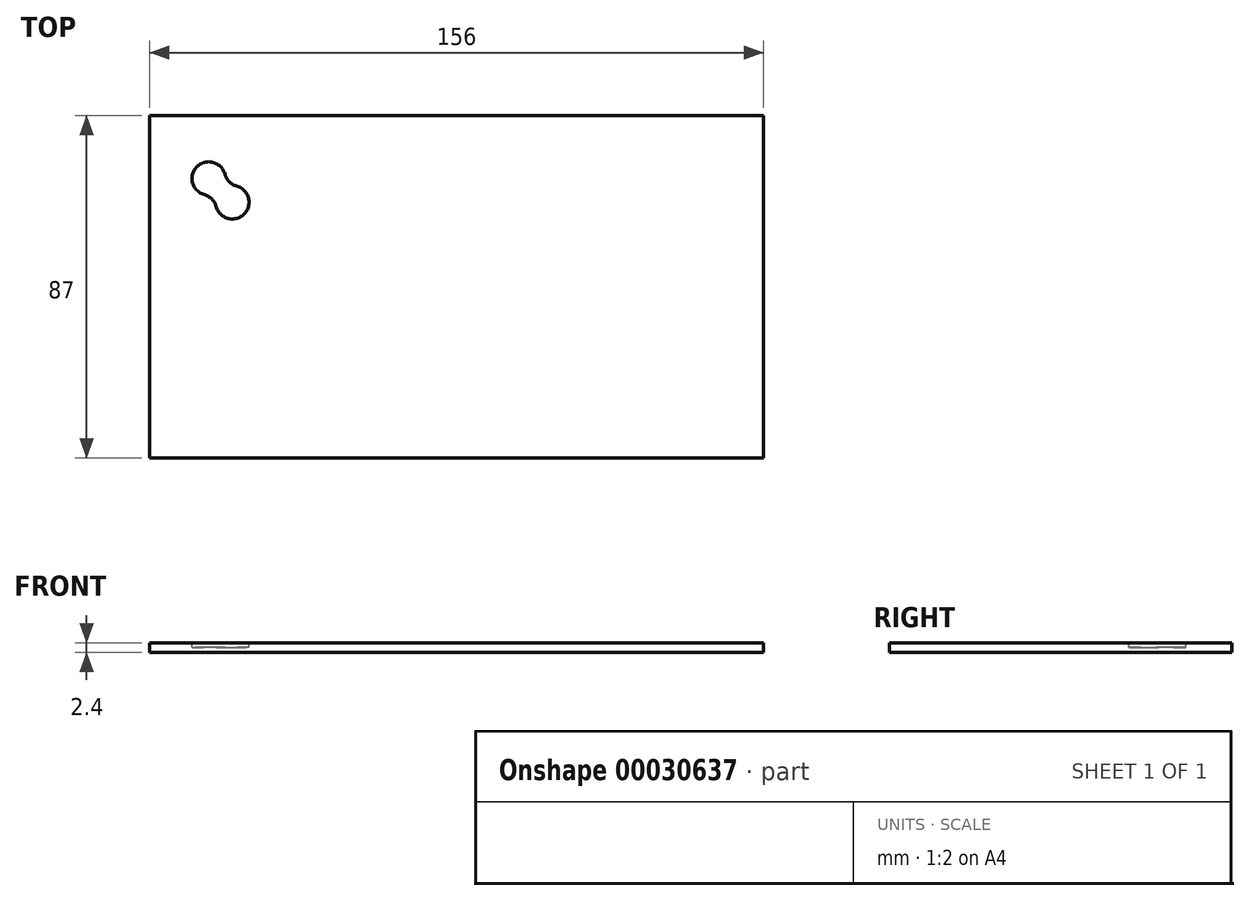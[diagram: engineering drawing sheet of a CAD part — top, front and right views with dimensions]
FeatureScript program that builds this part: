
annotation { "Feature Type Name" : "Feature", "Feature Type Description" : "" }
export const myFeature = defineFeature(function(context is Context, id is Id, definition is map)
    precondition{}
    {
        {
            var Q0;
            Q0=qCreatedBy(makeId("Top.planeOp"),FACE);
            var sketch = newSketch(context, id + "F0", { "sketchPlane" : qUnion([Q0])});
            skLineSegment(sketch, "E0.bottom", {"start": v(-75.67, 9.55) * mm, "end": v(80.33, 9.55) * mm});
            skLineSegment(sketch, "E0.top", {"start": v(-75.67, -77.45) * mm, "end": v(80.33, -77.45) * mm});
            skLineSegment(sketch, "E0.left", {"start": v(-75.67, 9.55) * mm, "end": v(-75.67, -77.45) * mm});
            skLineSegment(sketch, "E0.right", {"start": v(80.33, 9.55) * mm, "end": v(80.33, -77.45) * mm});
            skSolve(sketch);
        }
        {
            var Q0;
            Q0=qCreatedBy(makeId("Top.planeOp"),FACE);
            var sketch = newSketch(context, id + "F1", { "sketchPlane" : qUnion([Q0])});
            skArc(sketch, "E1", {"start": v(-58.78, -13.57) * mm, "mid": v(-51.67, -15.48) * mm, "end": v(-53.56, -8.37) * mm});
            skArc(sketch, "E2", {"start": v(-58.78, -13.57) * mm, "mid": v(-59.87, -11.66) * mm, "end": v(-61.78, -10.56) * mm});
            skArc(sketch, "E3", {"start": v(-56.56, -5.36) * mm, "mid": v(-55.47, -7.27) * mm, "end": v(-53.56, -8.37) * mm});
            skArc(sketch, "E4.trimOffspring", {"start": v(-56.56, -5.36) * mm, "mid": v(-63.67, -3.44) * mm, "end": v(-61.78, -10.56) * mm});
            skSolve(sketch);
        }
        {
            var Q0;
            Q0=makeQuery(id+"F0.imprint","IMPRINT",FACE,{"disambiguationData":[TD([[makeQuery(id+"F0.imprint","IMPRINT",EDGE,{"derivedFrom":sQuery(id+"F0.wireOp",EDGE,"E0.bottom")}),-1.0]])]});
            extrude(context, id + "F2", {"entities" : qUnion([Q0]), "oppositeDirection" : true, "depth" : 2.4 * mm});
        }
        {
            var Q0;
            Q0 = qSketchRegion(id + "F1", true);
            extrude(context, id + "F3", {"entities" : qUnion([Q0]), "operationType" : NewBodyOperationType.REMOVE, "oppositeDirection" : true, "depth" : 1.2 * mm});
        }
    });
